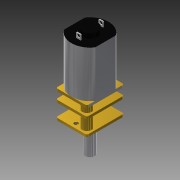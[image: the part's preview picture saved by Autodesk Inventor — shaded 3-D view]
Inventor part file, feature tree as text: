
AUTODESK INVENTOR PART (.ipt)
format: ipt  version: 2014 SP1 (Build 180222100, 222)  size: 249,856 bytes
history: native  units: mm
features: sketch x11, extrude x10, fillet x3, mirror x1, plane x1, hole x1
ambient origin geometry x8: Origin, YZ Plane, XZ Plane, XY Plane, X Axis, Y Axis, Z Axis, Center Point
bodies: Solid1 (feature_tree)
feature tree (27):
  extrude  "Extrusion1"  Depth=10.0mm
  extrude  "Extrusion2"  Depth=5.0mm
  extrude  "Extrusion3"  Depth=1.5mm
  extrude  "Extrusion4"  Depth=1.55mm
  fillet  "Fillet1"  Radius=1.65mm
  mirror  "Mirror1"
  extrude  "Extrusion5"  Depth=0.7mm
  extrude  "Extrusion6"  Depth=0.25mm
  plane  "Work Plane1"
  extrude  "Extrusion7"  Depth=0.8mm
  extrude  "Extrusion8"  Depth=2.15mm
  hole  "Hole1"  [1 undecoded]
  extrude  "Extrusion9"  Depth=8.2mm TaperAngle=0.0deg
  extrude  "Extrusion10"  Depth=0.8mm TaperAngle=0.0deg
  fillet  "Fillet2"  Radius=0.8mm
  fillet  "Fillet3"  Radius=4.5mm
  sketch  "Sketch1"  dims[d0=12.0mm d1=10.0mm]
  sketch  "Sketch2"  dims[d2=15.0mm d3=0.0mm d4=5.0mm]
  sketch  "Sketch3"  dims[d5=1.5mm d6=0.0mm d7=3.775mm]
  sketch  "Sketch4"  dims[d8=0.3mm d9=1.55mm d10=1.65mm d11=0.0mm]
  sketch  "Sketch5"  dims[d12=1.0mm d13=0.7mm]
  sketch  "Sketch6"  dims[d14=1.65mm d15=0.0mm d16=0.25mm]
  sketch  "Sketch7"  dims[d17=0.8mm d18=0.0mm d19=3.0mm]
  sketch  "Sketch8"  dims[d20=2.15mm d21=2.15mm]
  sketch  "Sketch9"  dims[d22=3.0mm d23=2.15mm]
  sketch  "Sketch10"  dims[d24=2.15mm d25=8.2mm d26=0.0mm]
  sketch  "Sketch11"  dims[d27=2.35mm d28=0.8mm d29=0.0mm d30=0.8mm d31=0.0mm d32=4.5mm d33=4.5mm d34=1.221mm d35=0.8mm d36=4.0mm d37=2.0mm d38=90.0deg d39=1.0mm d40=0.0mm d41=3.9mm d42=0.6mm d43=0.0mm d44=3.0mm d45=1.0mm d46=9.27mm d47=0.0mm d48=0.5mm d49=0.5mm]
note: 1 required parameter value undecoded (feature->parameter linkage not recoverable at this tier; creation-order binding heuristic only, values carry confidence <= 0.55)
